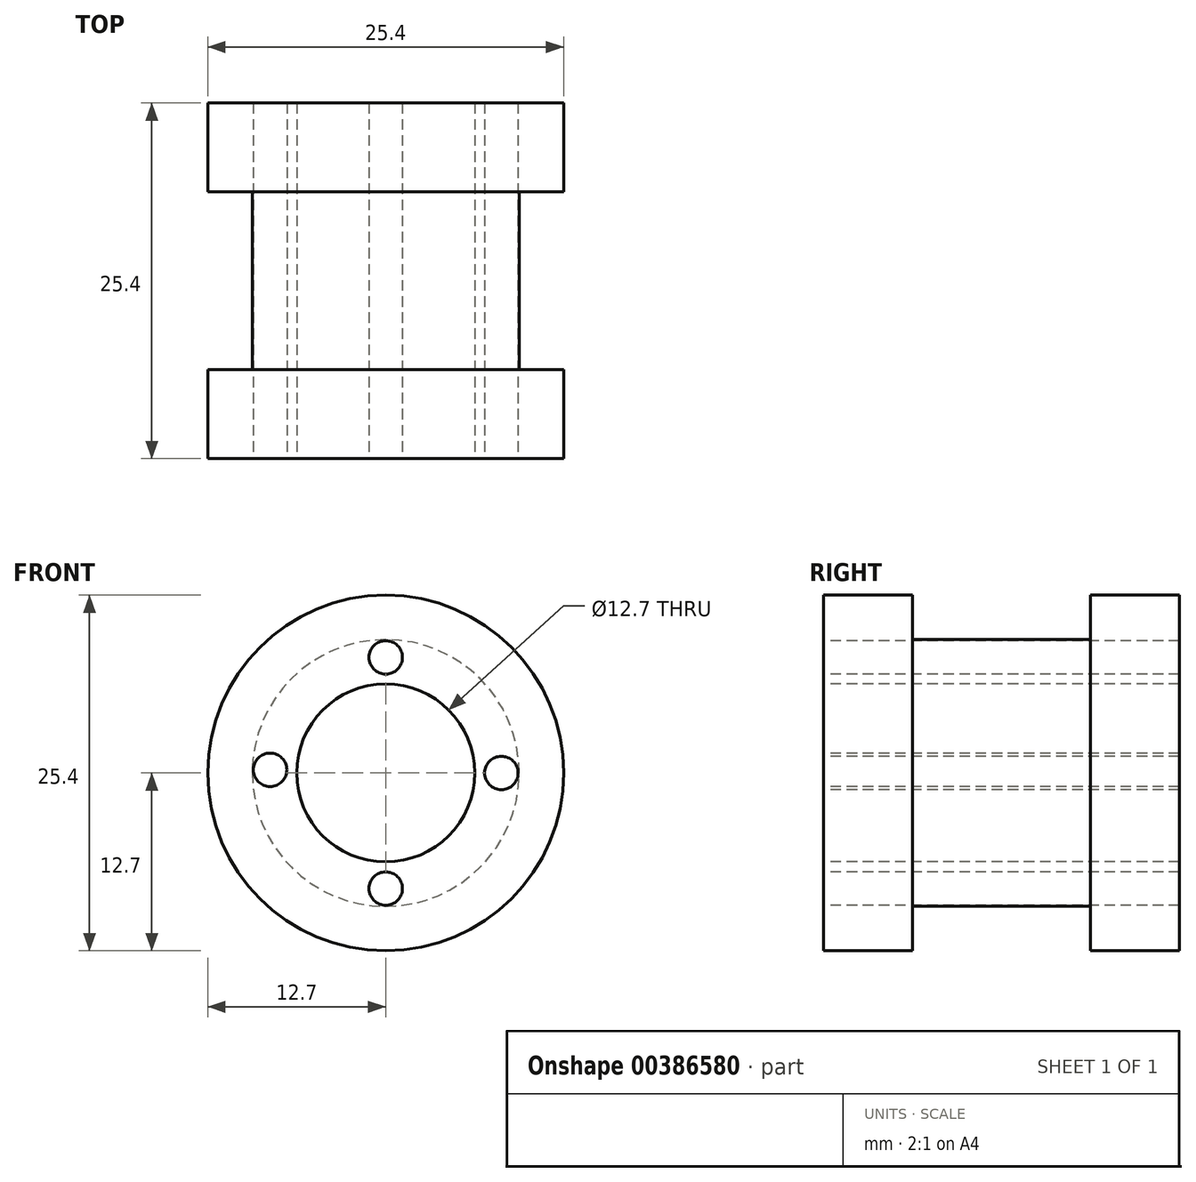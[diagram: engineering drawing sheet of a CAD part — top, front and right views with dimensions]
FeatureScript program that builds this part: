
annotation { "Feature Type Name" : "Feature", "Feature Type Description" : "" }
export const myFeature = defineFeature(function(context is Context, id is Id, definition is map)
    precondition{}
    {
        {
            var Q0;
            Q0=qCreatedBy(makeId("Front.planeOp"),FACE);
            var sketch = newSketch(context, id + "F0", { "sketchPlane" : qUnion([Q0])});
            skCircle(sketch, "E0", {"center": v(0, 0) * mm, "radius": 12.7 * mm});
            skSolve(sketch);
        }
        {
            var Q0;
            Q0 = qSketchRegion(id + "F0", true);
            extrude(context, id + "F1", {"entities" : qUnion([Q0]), "depth" : 6.35 * mm});
        }
        {
            var Q0;
            Q0=makeQuery(id+"F1.opExtrude","CAP_FACE",FACE,{"disambiguationData":[OSD([sQuery(id+"F0.wireOp",EDGE,"E0")])],"isStart":true});
            var sketch = newSketch(context, id + "F2", { "sketchPlane" : qUnion([Q0])});
            skCircle(sketch, "E1", {"center": v(0, 0) * mm, "radius": 9.53 * mm});
            skSolve(sketch);
        }
        {
            var Q0;
            Q0 = qSketchRegion(id + "F2", true);
            extrude(context, id + "F3", {"entities" : qUnion([Q0]), "operationType" : NewBodyOperationType.ADD, "depth" : 12.7 * mm});
        }
        {
            var Q0;
            Q0=makeQuery(id+"F3.opExtrude","CAP_FACE",FACE,{"disambiguationData":[OSD([sQuery(id+"F2.wireOp",EDGE,"E1")])],"isStart":false});
            var sketch = newSketch(context, id + "F4", { "sketchPlane" : qUnion([Q0])});
            skCircle(sketch, "E2", {"center": v(0, 0) * mm, "radius": 12.7 * mm});
            skSolve(sketch);
        }
        {
            var Q0;
            Q0 = qSketchRegion(id + "F4", true);
            extrude(context, id + "F5", {"entities" : qUnion([Q0]), "operationType" : NewBodyOperationType.ADD, "depth" : 6.35 * mm});
        }
        {
            var Q0;
            Q0=makeQuery(id+"F1.opExtrude","CAP_FACE",FACE,{"disambiguationData":[OSD([sQuery(id+"F0.wireOp",EDGE,"E0")])],"isStart":false});
            var sketch = newSketch(context, id + "F6", { "sketchPlane" : qUnion([Q0])});
            skPoint(sketch, "E3", {"position": v(0, 0) * mm});
            skPoint(sketch, "E4", {"position": v(0, 8.26) * mm});
            skPoint(sketch, "E5", {"position": v(8.26, 0) * mm});
            skPoint(sketch, "E6", {"position": v(-8.25, 0.23) * mm});
            skPoint(sketch, "E7", {"position": v(0, -8.26) * mm});
            skSolve(sketch);
        }
        {
            var Q0;
            Q0=sQuery(id+"F6.wireOp",VERTEX,"E3");
            var Q1;
            Q1=makeQuery(id+"F1.opExtrude","SWEPT_BODY",BODY,{"disambiguationData":[OSD([sQuery(id+"F0.wireOp",EDGE,"E0")])]});
            hole(context, id + "F7", {"style" : HoleStyle.SIMPLE, "endStyle" : HoleEndStyle.THROUGH, "holeDiameter" : 12.7 * mm, "isTappedThrough" : true, "tappedDepth" : 12.7 * mm, "tapClearance" : 3, "locations" : qUnion([Q0]), "scope" : qUnion([Q1])});
        }
        {
            var Q0;
            Q0=sQuery(id+"F6.wireOp",VERTEX,"E4");
            var Q1;
            Q1=sQuery(id+"F6.wireOp",VERTEX,"E6");
            var Q2;
            Q2=sQuery(id+"F6.wireOp",VERTEX,"E7");
            var Q3;
            Q3=sQuery(id+"F6.wireOp",VERTEX,"E5");
            var Q4;
            Q4=makeQuery(id+"F1.opExtrude","SWEPT_BODY",BODY,{"disambiguationData":[OSD([sQuery(id+"F0.wireOp",EDGE,"E0")])]});
            hole(context, id + "F8", {"style" : HoleStyle.SIMPLE, "endStyle" : HoleEndStyle.THROUGH, "holeDiameter" : 2.4 * mm, "isTappedThrough" : true, "tappedDepth" : 12.7 * mm, "tapClearance" : 3, "locations" : qUnion([Q0, Q1, Q2, Q3]), "scope" : qUnion([Q4])});
        }
    });
